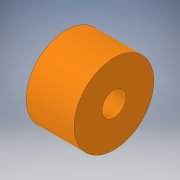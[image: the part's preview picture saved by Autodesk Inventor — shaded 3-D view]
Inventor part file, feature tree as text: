
AUTODESK INVENTOR PART (.ipt)
format: ipt  version: 2017 SP1 (Build 210196100, 196)  size: 95,744 bytes
history: native  units: in
note: dims shown in document units (in); Inventor stores cm internally (conversion verified against a paired STEP export)
features: extrude x1, sketch x1
ambient origin geometry x8: Origin, YZ Plane, XZ Plane, XY Plane, X Axis, Y Axis, Z Axis, Center Point
bodies: Solid1 (feature_tree)
feature tree (2):
  extrude  "Extrusion1"  Depth=0.75in
  sketch  "Sketch1"  dims[d0=0.375in d1=1.25in d2=0.75in d3=0.0in]
